# Revit family: en-halla-lumia-accessories-suspendedrfa (1)
name_source: partatom
category: Specialty Equipment
revit_build: Autodesk Revit 2017 (Build: 20160225_1515(x64)
units: mm (PartAtom-declared; Revit-internal decimal feet)

## family parameters
Cut with Voids When Loaded = No
Host = Face
OmniClass Number = 23.80.70.11.11
OmniClass Title = General Luminaries, Non Directional
Part Type = Normal
Room Calculation Point = No
Round Connector Dimension = Use Diameter
Shared = No

## types (5) — shared parameters
Assembly Code = D5020230
Colour of luminaire = Aluminium - anodised
Default Elevation = 1000 mm  [stored 3.28084 ft]
Lighting height = 36 mm  [stored 0.11811 ft]
Lighting length = 1000 mm  [stored 3.28084 ft]
Lighting width = 230 mm  [stored 0.754593 ft]
Manufacturer = HALLA
Material of luminaire = Aluminium
URL = http://www.halla.cz
Výška zavěšení maximální = 2000 mm  [stored 6.56168 ft]

## per-type parameters (varying)
| type | L | QR code | T | Tubus | X |
| 10-0001, E - profile for modules | No |  | No | Yes | No |
| 10-0011, E - body profile | No |  | No | Yes | No |
| 10-0003, E - joint L | Yes | http://file-system.ru | No | No | No |
| 10-0004, E - joint T | No |  | Yes | No | No |
| 10-0005, E - joint X | No |  | No | No | Yes |

note: [stored X ft] marks values corroborated as IEEE doubles in the binary element streams (Revit-internal decimal feet)
